# Revit family: Allure RFIDA w_cyl
name_source: partatom
category: Doors
units: mm (PartAtom-declared; Revit-internal decimal feet)

## family parameters
Always vertical = Yes
Cut with Voids When Loaded = No
Host = Wall
OmniClass Number = 23.30.10.14.14
OmniClass Title = Wood Passage Doors
Room Calculation Point = No
Shared = No

## types (2) — shared parameters
AAOS Adjacent Wall Placement = 102 mm
AAOS Door Configuration = SG
AAOS Door Elevation Type = WD
AAOS Door Finish Color = Red Oak 100 Clear
AAOS Door Finish Type = SRO
AAOS Door Material = Stain - ASSA ABLOY Wood Doors (GR) - SRO - Red Oak 100 Clear
AAOS Door Material Type = Wood
AAOS Door Panel Type = F
AAOS Family Version = 1.0
AAOS Frame Elevation Data = 3 Piece
AAOS Frame Elevation Type = HM
AAOS Frame Head Width = 51 mm
AAOS Frame Jamb Width = 51 mm
AAOS Frame Material = <By Category>
AAOS Frame Material Type = Hollow Metal
AAOS Frame Type = 3 Piece
AAOS Glass Material = Glass
AAOS No Panels = 1
AAOS Panel 1 Width = 914 mm
Analytic Construction = <None>
Assembly Code = C1020320
Description = Wood Door with Hollow Metal Frame
Door Panel Height = 2134 mm
Door Panel Width = 914 mm
Frame Height = 2184 mm
Frame Width = 1016 mm
Function = Interior
Height = 2134 mm
Leaf Width = 910 mm
Left Frame Width = 51 mm
Manufacturer = ASSA ABLOY
P1 Width = 965 mm
R1 Height = 2083 mm
Right Frame Width = 51 mm
Rough Height = 2172 mm
Rough Width = 991 mm
Show Door = Yes
Show Frame = Yes
Show Glass = Yes
Thickness = 44 mm
URL = www.OpeningsStudio.com
Width = 914 mm
zero-valued in all types: AAOS RO Spacing, Cost

## per-type parameters (varying)
| type | AAOS Library ID |
| Pull | d5e7c711-6214-4af3-8262-fb0559b2abca |
| Push | 779ace07-b5ad-4c57-a0d3-754d2b976ca6 |

note: column(s) folded — value = type name in every type: Model

## geometry (parser evidence)
native form markers: Sweep x30
no freeform markers — native parametric forms only
